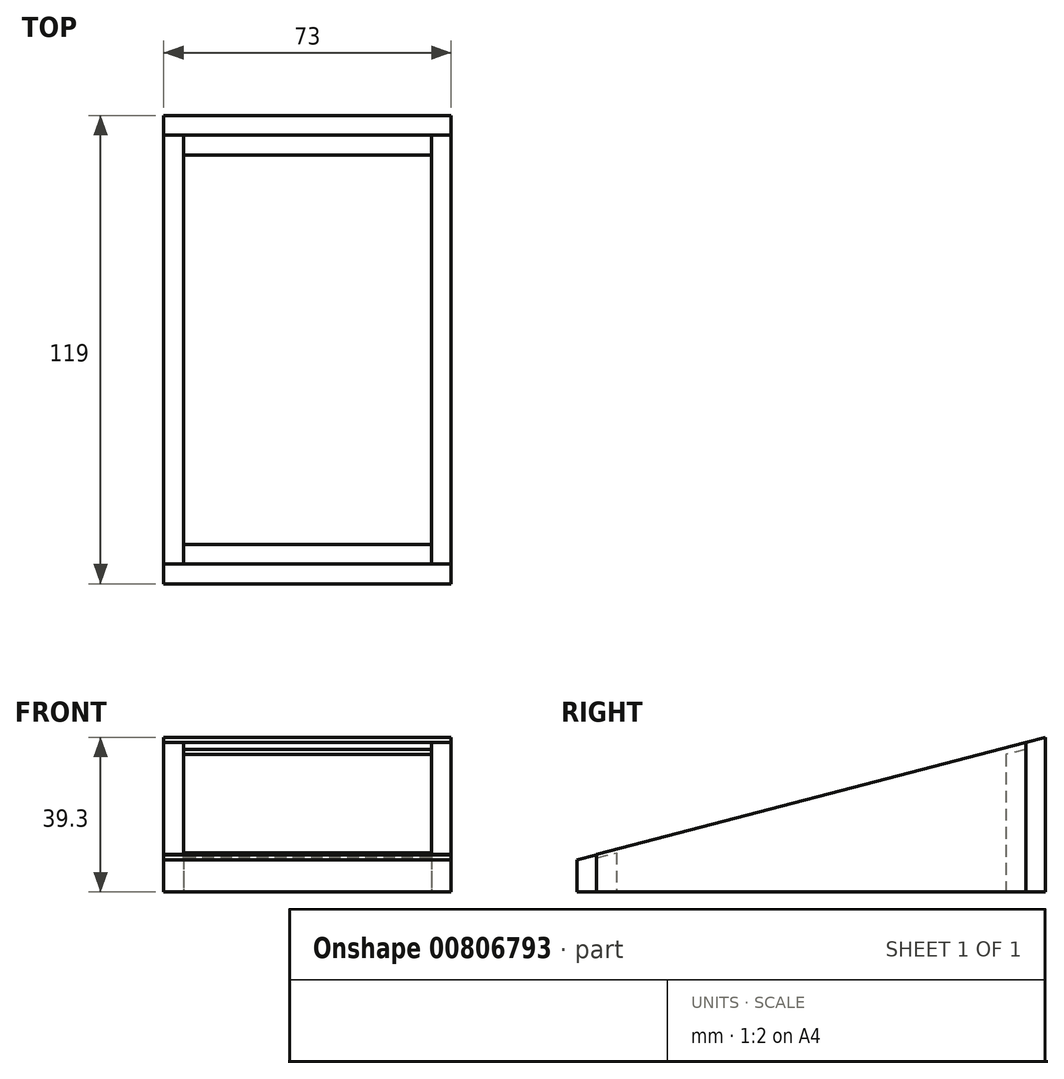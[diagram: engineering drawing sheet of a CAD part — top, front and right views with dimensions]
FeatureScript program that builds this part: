
annotation { "Feature Type Name" : "Feature", "Feature Type Description" : "" }
export const myFeature = defineFeature(function(context is Context, id is Id, definition is map)
    precondition{}
    {
        {
            var Q0;
            Q0=qCreatedBy(makeId("Top.planeOp"),FACE);
            var sketch = newSketch(context, id + "F0", { "sketchPlane" : qUnion([Q0])});
            skLineSegment(sketch, "E0", {"start": v(63, 0) * mm, "end": v(0, 0) * mm});
            skLineSegment(sketch, "E1", {"start": v(0, 0) * mm, "end": v(0, -109) * mm});
            skLineSegment(sketch, "E2", {"start": v(0, -109) * mm, "end": v(63, -109) * mm});
            skLineSegment(sketch, "E3", {"start": v(63, -109) * mm, "end": v(63, 0) * mm});
            skLineSegment(sketch, "E4", {"start": v(68, -114) * mm, "end": v(-5, -114) * mm});
            skLineSegment(sketch, "E5", {"start": v(-5, -114) * mm, "end": v(-5, 5) * mm});
            skLineSegment(sketch, "E6", {"start": v(-5, 5) * mm, "end": v(68, 5) * mm});
            skLineSegment(sketch, "E7", {"start": v(68, 5) * mm, "end": v(68, -114) * mm});
            skLineSegment(sketch, "E8", {"start": v(5, -5) * mm, "end": v(58, -5) * mm});
            skLineSegment(sketch, "E9", {"start": v(58, -5) * mm, "end": v(58, -104) * mm});
            skLineSegment(sketch, "E10", {"start": v(58, -104) * mm, "end": v(5, -104) * mm});
            skLineSegment(sketch, "E11", {"start": v(5, -104) * mm, "end": v(5, -5) * mm});
            skLineSegment(sketch, "E12", {"start": v(5, -104) * mm, "end": v(0, -104) * mm});
            skLineSegment(sketch, "E13", {"start": v(0, -109) * mm, "end": v(-5, -109) * mm});
            skLineSegment(sketch, "E14", {"start": v(58, -104) * mm, "end": v(63, -104) * mm});
            skLineSegment(sketch, "E15", {"start": v(63, -109) * mm, "end": v(68, -109) * mm});
            skLineSegment(sketch, "E16", {"start": v(63, 0) * mm, "end": v(68, 0) * mm});
            skLineSegment(sketch, "E17", {"start": v(58, -5) * mm, "end": v(63, -5) * mm});
            skLineSegment(sketch, "E18", {"start": v(0, 0) * mm, "end": v(-5, 0) * mm});
            skLineSegment(sketch, "E19", {"start": v(5, -5) * mm, "end": v(0, -5) * mm});
            skSolve(sketch);
        }
        {
            var Q0;
            Q0=makeQuery(id+"F0.imprint","IMPRINT",FACE,{"disambiguationData":[TD([[makeQuery(id+"F0.imprint","IMPRINT",EDGE,{"derivedFrom":sQuery(id+"F0.wireOp",EDGE,"E0")}),1.0]])]});
            extrude(context, id + "F1", {"entities" : qUnion([Q0]), "depth" : 36.26 * mm, "offsetDistance" : 25 * mm});
        }
        {
            var Q0;
            Q0=makeQuery(id+"F0.imprint","IMPRINT",FACE,{"disambiguationData":[TD([[makeQuery(id+"F0.imprint","IMPRINT",EDGE,{"derivedFrom":sQuery(id+"F0.wireOp",EDGE,"E0")}),-1.0]])]});
            extrude(context, id + "F2", {"entities" : qUnion([Q0]), "operationType" : NewBodyOperationType.ADD, "depth" : 39.3 * mm, "offsetDistance" : 25 * mm});
        }
        {
            var Q0;
            Q0=makeQuery(id+"F0.imprint","IMPRINT",FACE,{"disambiguationData":[TD([[makeQuery(id+"F0.imprint","IMPRINT",EDGE,{"derivedFrom":sQuery(id+"F0.wireOp",EDGE,"E2")}),-1.0]])]});
            extrude(context, id + "F3", {"entities" : qUnion([Q0]), "depth" : 9.5 * mm, "offsetDistance" : 25 * mm});
        }
        {
            var Q0;
            {var subQ1=sQuery(id+"F0.wireOp",EDGE,"E2");Q0=makeQuery(id+"F0.imprint","IMPRINT",FACE,{"disambiguationData":[TD([[makeQuery(id+"F0.imprint","IMPRINT",EDGE,{"derivedFrom":subQ1}),1.0]])]});}
            extrude(context, id + "F4", {"entities" : qUnion([Q0]), "depth" : 10 * mm, "offsetDistance" : 25 * mm});
        }
        {
            var Q0;
            {var subQ0=sQuery(id+"F0.wireOp",EDGE,"E15");Q0=makeQuery(id+"F0.imprint","IMPRINT",FACE,{"disambiguationData":[TD([[makeQuery(id+"F0.imprint","IMPRINT",EDGE,{"derivedFrom":subQ0}),1.0]])]});}
            var Q1;
            {var subQ0=sQuery(id+"F0.wireOp",EDGE,"E13");Q1=makeQuery(id+"F0.imprint","IMPRINT",FACE,{"disambiguationData":[TD([[makeQuery(id+"F0.imprint","IMPRINT",EDGE,{"derivedFrom":subQ0}),-1.0]])]});}
            var Q2;
            Q2=makeQuery(id+"F1.opExtrude","SWEPT_BODY",BODY,{"disambiguationData":[OSD([sQuery(id+"F0.wireOp",EDGE,"E0"),sQuery(id+"F0.wireOp",EDGE,"E1"),sQuery(id+"F0.wireOp",EDGE,"E3"),sQuery(id+"F0.wireOp",EDGE,"E8"),sQuery(id+"F0.wireOp",EDGE,"E17"),sQuery(id+"F0.wireOp",EDGE,"E19")])]});
            extrude(context, id + "F5", {"entities" : qUnion([Q0, Q1]), "depth" : 38 * mm, "endBoundEntityBody" : qUnion([Q2]), "offsetDistance" : 25 * mm});
        }
        {
            var Q0;
            Q0=makeQuery(id+"F5.opExtrude","CAP_EDGE",EDGE,{"disambiguationData":[OSD([sQuery(id+"F0.wireOp",EDGE,"E15")])],"isStart":false});
            chamfer(context, id + "F6", {"entities" : qUnion([Q0]), "chamferType" : ChamferType.OFFSET_ANGLE, "width" : 109 * mm, "oppositeDirection" : false, "angle" : 14.65 * degree, "tangentPropagation" : true});
        }
        {
            var Q0;
            Q0=makeQuery(id+"F3.opExtrude","CAP_EDGE",EDGE,{"disambiguationData":[OSD([sQuery(id+"F0.wireOp",EDGE,"E4")])],"isStart":false});
            var Q1;
            Q1=makeQuery(id+"F2.opExtrude","CAP_EDGE",EDGE,{"disambiguationData":[OSD([sQuery(id+"F0.wireOp",EDGE,"E0"),sQuery(id+"F0.wireOp",EDGE,"E16"),sQuery(id+"F0.wireOp",EDGE,"E18")])],"isStart":false});
            chamfer(context, id + "F7", {"entities" : qUnion([Q0, Q1]), "chamferType" : ChamferType.OFFSET_ANGLE, "width" : 5 * mm, "oppositeDirection" : true, "angle" : 14.65 * degree, "tangentPropagation" : true});
        }
        {
            var Q0;
            Q0=makeQuery(id+"F1.opExtrude","CAP_EDGE",EDGE,{"disambiguationData":[OSD([sQuery(id+"F0.wireOp",EDGE,"E8"),sQuery(id+"F0.wireOp",EDGE,"E17"),sQuery(id+"F0.wireOp",EDGE,"E19")])],"isStart":false});
            var Q1;
            Q1=makeQuery(id+"F4.opExtrude","CAP_EDGE",EDGE,{"disambiguationData":[OSD([sQuery(id+"F0.wireOp",EDGE,"E2")])],"isStart":false});
            chamfer(context, id + "F8", {"entities" : qUnion([Q0, Q1]), "chamferType" : ChamferType.OFFSET_ANGLE, "width" : 5 * mm, "oppositeDirection" : false, "angle" : 14.65 * degree, "tangentPropagation" : true});
        }
        {
            var Q0;
            Q0=makeQuery(id+"F5.opExtrude","CAP_EDGE",EDGE,{"disambiguationData":[OSD([sQuery(id+"F0.wireOp",EDGE,"E13")])],"isStart":false});
            chamfer(context, id + "F9", {"entities" : qUnion([Q0]), "chamferType" : ChamferType.OFFSET_ANGLE, "width" : 109 * mm, "oppositeDirection" : true, "angle" : 14.65 * degree, "tangentPropagation" : true});
        }
    });
